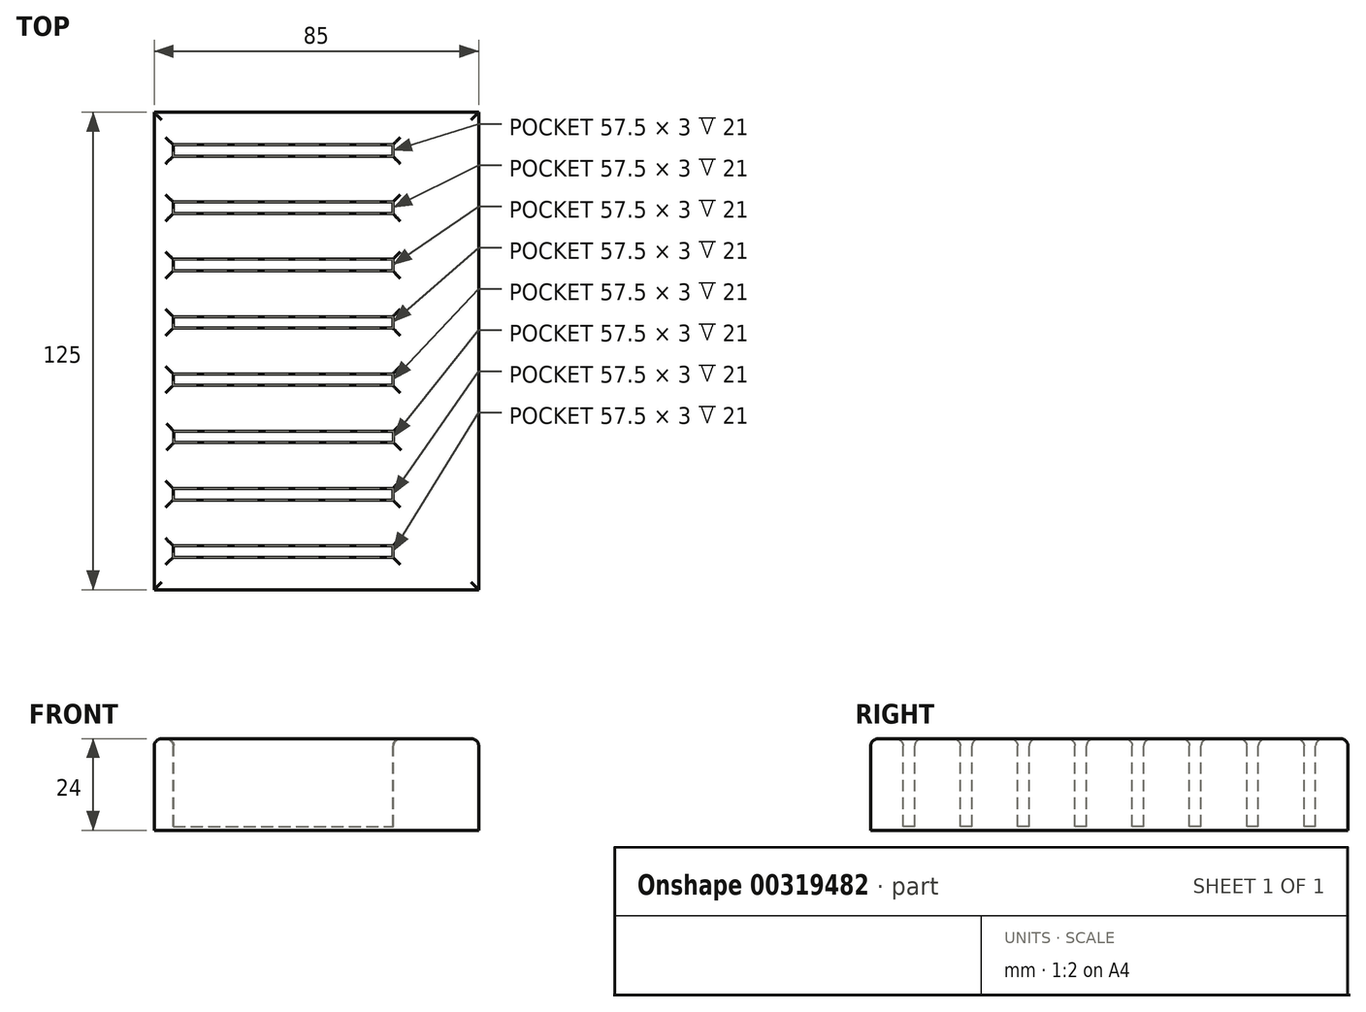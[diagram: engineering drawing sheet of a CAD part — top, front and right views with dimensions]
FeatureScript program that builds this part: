
annotation { "Feature Type Name" : "Feature", "Feature Type Description" : "" }
export const myFeature = defineFeature(function(context is Context, id is Id, definition is map)
    precondition{}
    {
        {
            var Q0;
            Q0=qCreatedBy(makeId("Top.planeOp"),FACE);
            var sketch = newSketch(context, id + "F0", { "sketchPlane" : qUnion([Q0])});
            skLineSegment(sketch, "E0.bottom", {"start": v(-49.85, 96.63) * mm, "end": v(35.15, 96.63) * mm});
            skLineSegment(sketch, "E0.top", {"start": v(-49.85, -28.37) * mm, "end": v(35.15, -28.37) * mm});
            skLineSegment(sketch, "E0.left", {"start": v(-49.85, 96.63) * mm, "end": v(-49.85, -28.37) * mm});
            skLineSegment(sketch, "E0.right", {"start": v(35.15, 96.63) * mm, "end": v(35.15, -28.37) * mm});
            skSolve(sketch);
        }
        {
            var Q0;
            Q0=makeQuery(id+"F0.imprint","IMPRINT",FACE,{"disambiguationData":[TD([[makeQuery(id+"F0.imprint","IMPRINT",EDGE,{"derivedFrom":sQuery(id+"F0.wireOp",EDGE,"E0.bottom")}),-1.0]])]});
            var Q1;
            Q1=makeQuery(id+"F0.imprint","IMPRINT",FACE,{"disambiguationData":[TD([[makeQuery(id+"F0.imprint","IMPRINT",EDGE,{"derivedFrom":sQuery(id+"F0.wireOp",EDGE,"eXpO4zti-W6eb-gkUP-Bc0d-zbJJjk6ygzeg.bottom")}),-1.0]])]});
            var Q2;
            Q2=makeQuery(id+"F0.imprint","IMPRINT",FACE,{"disambiguationData":[TD([[makeQuery(id+"F0.imprint","IMPRINT",EDGE,{"derivedFrom":sQuery(id+"F0.wireOp",EDGE,"IiJkesfC-iyIp-GpGT-9vFS-BzQ84R5pHUzr.bottom")}),-1.0]])]});
            extrude(context, id + "F1", {"entities" : qUnion([Q0, Q1, Q2]), "depth" : 24 * mm});
        }
        {
            var Q0;
            Q0=makeQuery(id+"F1.opExtrude","CAP_FACE",FACE,{"disambiguationData":[OSD([sQuery(id+"F0.wireOp",EDGE,"E0.bottom"),sQuery(id+"F0.wireOp",EDGE,"E0.top"),sQuery(id+"F0.wireOp",EDGE,"E0.left"),sQuery(id+"F0.wireOp",EDGE,"E0.right")])],"isStart":false});
            var sketch = newSketch(context, id + "F2", { "sketchPlane" : qUnion([Q0])});
            skLineSegment(sketch, "E1.bottom", {"start": v(-44.85, -16.87) * mm, "end": v(12.65, -16.87) * mm});
            skLineSegment(sketch, "E1.top", {"start": v(-44.85, -19.87) * mm, "end": v(12.65, -19.87) * mm});
            skLineSegment(sketch, "E1.left", {"start": v(-44.85, -16.87) * mm, "end": v(-44.85, -19.87) * mm});
            skLineSegment(sketch, "E1.right", {"start": v(12.65, -16.87) * mm, "end": v(12.65, -19.87) * mm});
            skLineSegment(sketch, "E2.bottom", {"start": v(-44.87, -1.87) * mm, "end": v(12.63, -1.87) * mm});
            skLineSegment(sketch, "E2.top", {"start": v(-44.87, -4.87) * mm, "end": v(12.63, -4.87) * mm});
            skLineSegment(sketch, "E2.left", {"start": v(-44.87, -1.87) * mm, "end": v(-44.87, -4.87) * mm});
            skLineSegment(sketch, "E2.right", {"start": v(12.63, -1.87) * mm, "end": v(12.63, -4.87) * mm});
            skLineSegment(sketch, "E3.bottom", {"start": v(-44.66, 13.13) * mm, "end": v(12.84, 13.13) * mm});
            skLineSegment(sketch, "E3.top", {"start": v(-44.66, 10.13) * mm, "end": v(12.84, 10.13) * mm});
            skLineSegment(sketch, "E3.left", {"start": v(-44.66, 13.13) * mm, "end": v(-44.66, 10.13) * mm});
            skLineSegment(sketch, "E3.right", {"start": v(12.84, 13.13) * mm, "end": v(12.84, 10.13) * mm});
            skLineSegment(sketch, "E4.bottom", {"start": v(-44.85, 28.13) * mm, "end": v(12.65, 28.13) * mm});
            skLineSegment(sketch, "E4.top", {"start": v(-44.85, 25.13) * mm, "end": v(12.65, 25.13) * mm});
            skLineSegment(sketch, "E4.left", {"start": v(-44.85, 28.13) * mm, "end": v(-44.85, 25.13) * mm});
            skLineSegment(sketch, "E4.right", {"start": v(12.65, 28.13) * mm, "end": v(12.65, 25.13) * mm});
            skLineSegment(sketch, "E5.bottom", {"start": v(-44.85, 43.13) * mm, "end": v(12.65, 43.13) * mm});
            skLineSegment(sketch, "E5.top", {"start": v(-44.85, 40.13) * mm, "end": v(12.65, 40.13) * mm});
            skLineSegment(sketch, "E5.left", {"start": v(-44.85, 43.13) * mm, "end": v(-44.85, 40.13) * mm});
            skLineSegment(sketch, "E5.right", {"start": v(12.65, 43.13) * mm, "end": v(12.65, 40.13) * mm});
            skLineSegment(sketch, "E6.bottom", {"start": v(-44.85, 58.13) * mm, "end": v(12.65, 58.13) * mm});
            skLineSegment(sketch, "E6.top", {"start": v(-44.85, 55.13) * mm, "end": v(12.65, 55.13) * mm});
            skLineSegment(sketch, "E6.left", {"start": v(-44.85, 58.13) * mm, "end": v(-44.85, 55.13) * mm});
            skLineSegment(sketch, "E6.right", {"start": v(12.65, 58.13) * mm, "end": v(12.65, 55.13) * mm});
            skLineSegment(sketch, "E7.bottom", {"start": v(-44.85, 73.13) * mm, "end": v(12.65, 73.13) * mm});
            skLineSegment(sketch, "E7.top", {"start": v(-44.85, 70.13) * mm, "end": v(12.65, 70.13) * mm});
            skLineSegment(sketch, "E7.left", {"start": v(-44.85, 73.13) * mm, "end": v(-44.85, 70.13) * mm});
            skLineSegment(sketch, "E7.right", {"start": v(12.65, 73.13) * mm, "end": v(12.65, 70.13) * mm});
            skLineSegment(sketch, "E8.bottom", {"start": v(-44.85, 88.13) * mm, "end": v(12.65, 88.13) * mm});
            skLineSegment(sketch, "E8.top", {"start": v(-44.85, 85.13) * mm, "end": v(12.65, 85.13) * mm});
            skLineSegment(sketch, "E8.left", {"start": v(-44.85, 88.13) * mm, "end": v(-44.85, 85.13) * mm});
            skLineSegment(sketch, "E8.right", {"start": v(12.65, 88.13) * mm, "end": v(12.65, 85.13) * mm});
            skSolve(sketch);
        }
        {
            var Q0;
            Q0=makeQuery(id+"F2.imprint","IMPRINT",FACE,{"disambiguationData":[TD([[makeQuery(id+"F2.imprint","IMPRINT",EDGE,{"derivedFrom":sQuery(id+"F2.wireOp",EDGE,"yj92iIYZ-7Uuq-LLpB-xCTO-jwhjS4Wwiwas.bottom")}),-1.0]])]});
            var Q1;
            Q1=makeQuery(id+"F2.imprint","IMPRINT",FACE,{"disambiguationData":[TD([[makeQuery(id+"F2.imprint","IMPRINT",EDGE,{"derivedFrom":sQuery(id+"F2.wireOp",EDGE,"E1.bottom")}),-1.0]])]});
            var Q2;
            Q2=makeQuery(id+"F2.imprint","IMPRINT",FACE,{"disambiguationData":[TD([[makeQuery(id+"F2.imprint","IMPRINT",EDGE,{"derivedFrom":sQuery(id+"F2.wireOp",EDGE,"E2.bottom")}),-1.0]])]});
            var Q3;
            Q3=makeQuery(id+"F2.imprint","IMPRINT",FACE,{"disambiguationData":[TD([[makeQuery(id+"F2.imprint","IMPRINT",EDGE,{"derivedFrom":sQuery(id+"F2.wireOp",EDGE,"6c3d6b7c-aaf7-4bf9-aa00-7a1dd3ff97cf.bottom")}),-1.0]])]});
            var Q4;
            Q4=makeQuery(id+"F2.imprint","IMPRINT",FACE,{"disambiguationData":[TD([[makeQuery(id+"F2.imprint","IMPRINT",EDGE,{"derivedFrom":sQuery(id+"F2.wireOp",EDGE,"50188bc1-ddcb-4dd7-b74a-52671ef0af12.bottom")}),-1.0]])]});
            var Q5;
            Q5=makeQuery(id+"F2.imprint","IMPRINT",FACE,{"disambiguationData":[TD([[makeQuery(id+"F2.imprint","IMPRINT",EDGE,{"derivedFrom":sQuery(id+"F2.wireOp",EDGE,"40c54da7-0a9d-487e-a4c4-20ab9cb4bac7.bottom")}),-1.0]])]});
            var Q6;
            Q6=makeQuery(id+"F2.imprint","IMPRINT",FACE,{"disambiguationData":[TD([[makeQuery(id+"F2.imprint","IMPRINT",EDGE,{"derivedFrom":sQuery(id+"F2.wireOp",EDGE,"2c54d664-a705-4687-aeb6-1d6c2977d349.bottom")}),-1.0]])]});
            var Q7;
            Q7=makeQuery(id+"F2.imprint","IMPRINT",FACE,{"disambiguationData":[TD([[makeQuery(id+"F2.imprint","IMPRINT",EDGE,{"derivedFrom":sQuery(id+"F2.wireOp",EDGE,"37cae19a-1d6e-44c9-97dd-f8e5000e89ab.bottom")}),-1.0]])]});
            var Q8;
            Q8=makeQuery(id+"F2.imprint","IMPRINT",FACE,{"disambiguationData":[TD([[makeQuery(id+"F2.imprint","IMPRINT",EDGE,{"derivedFrom":sQuery(id+"F2.wireOp",EDGE,"b65af77c-a413-450f-8f38-1bad91a99a45.bottom")}),-1.0]])]});
            var Q9;
            Q9=makeQuery(id+"F2.imprint","IMPRINT",FACE,{"disambiguationData":[TD([[makeQuery(id+"F2.imprint","IMPRINT",EDGE,{"derivedFrom":sQuery(id+"F2.wireOp",EDGE,"7d05ea80-09af-4c06-bbdd-2276bf2f09b7.bottom")}),-1.0]])]});
            var Q10;
            Q10=makeQuery(id+"F2.imprint","IMPRINT",FACE,{"disambiguationData":[TD([[makeQuery(id+"F2.imprint","IMPRINT",EDGE,{"derivedFrom":sQuery(id+"F2.wireOp",EDGE,"01eb7785-34fb-4985-9cad-6e3e3be28db8.bottom")}),-1.0]])]});
            var Q11;
            Q11=makeQuery(id+"F2.imprint","IMPRINT",FACE,{"disambiguationData":[TD([[makeQuery(id+"F2.imprint","IMPRINT",EDGE,{"derivedFrom":sQuery(id+"F2.wireOp",EDGE,"7e82bba3-7e2f-4ee3-9ea2-689606380510.bottom")}),-1.0]])]});
            var Q12;
            Q12=makeQuery(id+"F2.imprint","IMPRINT",FACE,{"disambiguationData":[TD([[makeQuery(id+"F2.imprint","IMPRINT",EDGE,{"derivedFrom":sQuery(id+"F2.wireOp",EDGE,"E3.bottom")}),-1.0]])]});
            var Q13;
            Q13=makeQuery(id+"F2.imprint","IMPRINT",FACE,{"disambiguationData":[TD([[makeQuery(id+"F2.imprint","IMPRINT",EDGE,{"derivedFrom":sQuery(id+"F2.wireOp",EDGE,"E4.bottom")}),-1.0]])]});
            var Q14;
            Q14=makeQuery(id+"F2.imprint","IMPRINT",FACE,{"disambiguationData":[TD([[makeQuery(id+"F2.imprint","IMPRINT",EDGE,{"derivedFrom":sQuery(id+"F2.wireOp",EDGE,"E5.bottom")}),-1.0]])]});
            var Q15;
            Q15=makeQuery(id+"F2.imprint","IMPRINT",FACE,{"disambiguationData":[TD([[makeQuery(id+"F2.imprint","IMPRINT",EDGE,{"derivedFrom":sQuery(id+"F2.wireOp",EDGE,"E6.bottom")}),-1.0]])]});
            var Q16;
            Q16=makeQuery(id+"F2.imprint","IMPRINT",FACE,{"disambiguationData":[TD([[makeQuery(id+"F2.imprint","IMPRINT",EDGE,{"derivedFrom":sQuery(id+"F2.wireOp",EDGE,"E7.bottom")}),-1.0]])]});
            var Q17;
            Q17=makeQuery(id+"F2.imprint","IMPRINT",FACE,{"disambiguationData":[TD([[makeQuery(id+"F2.imprint","IMPRINT",EDGE,{"derivedFrom":sQuery(id+"F2.wireOp",EDGE,"E8.bottom")}),-1.0]])]});
            var Q18;
            Q18=makeQuery(id+"F2.imprint","IMPRINT",FACE,{"disambiguationData":[TD([[makeQuery(id+"F2.imprint","IMPRINT",EDGE,{"derivedFrom":sQuery(id+"F2.wireOp",EDGE,"efc62570-a1f0-4d1b-bca0-e349addd9173.bottom")}),-1.0]])]});
            var Q19;
            Q19=makeQuery(id+"F2.imprint","IMPRINT",FACE,{"disambiguationData":[TD([[makeQuery(id+"F2.imprint","IMPRINT",EDGE,{"derivedFrom":sQuery(id+"F2.wireOp",EDGE,"dca9b81b-4f38-4141-b403-f49ceaf93926.bottom")}),-1.0]])]});
            extrude(context, id + "F3", {"entities" : qUnion([Q0, Q1, Q2, Q3, Q4, Q5, Q6, Q7, Q8, Q9, Q10, Q11, Q12, Q13, Q14, Q15, Q16, Q17, Q18, Q19]), "operationType" : NewBodyOperationType.REMOVE, "oppositeDirection" : true, "depth" : 23 * mm});
        }
        {
            var Q0;
            Q0=makeQuery(id+"F3.boolean.opBoolean","COPY",EDGE,{"derivedFrom":makeQuery(id+"F3.opExtrude","CAP_EDGE",EDGE,{"disambiguationData":[OSD([sQuery(id+"F2.wireOp",EDGE,"E1.top")])],"isStart":true})});
            var Q1;
            Q1=makeQuery(id+"F3.boolean.opBoolean","COPY",EDGE,{"derivedFrom":makeQuery(id+"F3.opExtrude","CAP_EDGE",EDGE,{"disambiguationData":[OSD([sQuery(id+"F2.wireOp",EDGE,"E1.bottom")])],"isStart":true})});
            var Q2;
            Q2=makeQuery(id+"F3.boolean.opBoolean","COPY",EDGE,{"derivedFrom":makeQuery(id+"F3.opExtrude","CAP_EDGE",EDGE,{"disambiguationData":[OSD([sQuery(id+"F2.wireOp",EDGE,"E1.right")])],"isStart":true})});
            var Q3;
            Q3=makeQuery(id+"F3.boolean.opBoolean","COPY",EDGE,{"derivedFrom":makeQuery(id+"F3.opExtrude","CAP_EDGE",EDGE,{"disambiguationData":[OSD([sQuery(id+"F2.wireOp",EDGE,"E1.left")])],"isStart":true})});
            var Q4;
            Q4=makeQuery(id+"F3.boolean.opBoolean","COPY",EDGE,{"derivedFrom":makeQuery(id+"F3.opExtrude","CAP_EDGE",EDGE,{"disambiguationData":[OSD([sQuery(id+"F2.wireOp",EDGE,"yj92iIYZ-7Uuq-LLpB-xCTO-jwhjS4Wwiwas.bottom")])],"isStart":true})});
            var Q5;
            Q5=makeQuery(id+"F3.boolean.opBoolean","COPY",EDGE,{"derivedFrom":makeQuery(id+"F3.opExtrude","CAP_EDGE",EDGE,{"disambiguationData":[OSD([sQuery(id+"F2.wireOp",EDGE,"yj92iIYZ-7Uuq-LLpB-xCTO-jwhjS4Wwiwas.top")])],"isStart":true})});
            var Q6;
            Q6=makeQuery(id+"F3.boolean.opBoolean","COPY",EDGE,{"derivedFrom":makeQuery(id+"F3.opExtrude","CAP_EDGE",EDGE,{"disambiguationData":[OSD([sQuery(id+"F2.wireOp",EDGE,"yj92iIYZ-7Uuq-LLpB-xCTO-jwhjS4Wwiwas.left")])],"isStart":true})});
            var Q7;
            Q7=makeQuery(id+"F3.boolean.opBoolean","COPY",EDGE,{"derivedFrom":makeQuery(id+"F3.opExtrude","CAP_EDGE",EDGE,{"disambiguationData":[OSD([sQuery(id+"F2.wireOp",EDGE,"yj92iIYZ-7Uuq-LLpB-xCTO-jwhjS4Wwiwas.right")])],"isStart":true})});
            var Q8;
            Q8=makeQuery(id+"F3.boolean.opBoolean","COPY",EDGE,{"derivedFrom":makeQuery(id+"F3.opExtrude","CAP_EDGE",EDGE,{"disambiguationData":[OSD([sQuery(id+"F2.wireOp",EDGE,"E2.bottom")])],"isStart":true})});
            var Q9;
            Q9=makeQuery(id+"F3.boolean.opBoolean","COPY",EDGE,{"derivedFrom":makeQuery(id+"F3.opExtrude","CAP_EDGE",EDGE,{"disambiguationData":[OSD([sQuery(id+"F2.wireOp",EDGE,"E2.top")])],"isStart":true})});
            var Q10;
            Q10=makeQuery(id+"F3.boolean.opBoolean","COPY",EDGE,{"derivedFrom":makeQuery(id+"F3.opExtrude","CAP_EDGE",EDGE,{"disambiguationData":[OSD([sQuery(id+"F2.wireOp",EDGE,"E2.left")])],"isStart":true})});
            var Q11;
            Q11=makeQuery(id+"F3.boolean.opBoolean","COPY",EDGE,{"derivedFrom":makeQuery(id+"F3.opExtrude","CAP_EDGE",EDGE,{"disambiguationData":[OSD([sQuery(id+"F2.wireOp",EDGE,"E2.right")])],"isStart":true})});
            var Q12;
            Q12=makeQuery(id+"F3.boolean.opBoolean","COPY",EDGE,{"derivedFrom":makeQuery(id+"F3.opExtrude","CAP_EDGE",EDGE,{"disambiguationData":[OSD([sQuery(id+"F2.wireOp",EDGE,"6c3d6b7c-aaf7-4bf9-aa00-7a1dd3ff97cf.left")])],"isStart":true})});
            var Q13;
            Q13=makeQuery(id+"F3.boolean.opBoolean","COPY",EDGE,{"derivedFrom":makeQuery(id+"F3.opExtrude","CAP_EDGE",EDGE,{"disambiguationData":[OSD([sQuery(id+"F2.wireOp",EDGE,"6c3d6b7c-aaf7-4bf9-aa00-7a1dd3ff97cf.bottom")])],"isStart":true})});
            var Q14;
            Q14=makeQuery(id+"F3.boolean.opBoolean","COPY",EDGE,{"derivedFrom":makeQuery(id+"F3.opExtrude","CAP_EDGE",EDGE,{"disambiguationData":[OSD([sQuery(id+"F2.wireOp",EDGE,"6c3d6b7c-aaf7-4bf9-aa00-7a1dd3ff97cf.right")])],"isStart":true})});
            var Q15;
            Q15=makeQuery(id+"F3.boolean.opBoolean","COPY",EDGE,{"derivedFrom":makeQuery(id+"F3.opExtrude","CAP_EDGE",EDGE,{"disambiguationData":[OSD([sQuery(id+"F2.wireOp",EDGE,"6c3d6b7c-aaf7-4bf9-aa00-7a1dd3ff97cf.top")])],"isStart":true})});
            var Q16;
            Q16=makeQuery(id+"F3.boolean.opBoolean","COPY",EDGE,{"derivedFrom":makeQuery(id+"F3.opExtrude","CAP_EDGE",EDGE,{"disambiguationData":[OSD([sQuery(id+"F2.wireOp",EDGE,"50188bc1-ddcb-4dd7-b74a-52671ef0af12.top")])],"isStart":true})});
            var Q17;
            Q17=makeQuery(id+"F3.boolean.opBoolean","COPY",EDGE,{"derivedFrom":makeQuery(id+"F3.opExtrude","CAP_EDGE",EDGE,{"disambiguationData":[OSD([sQuery(id+"F2.wireOp",EDGE,"50188bc1-ddcb-4dd7-b74a-52671ef0af12.left")])],"isStart":true})});
            var Q18;
            Q18=makeQuery(id+"F3.boolean.opBoolean","COPY",EDGE,{"derivedFrom":makeQuery(id+"F3.opExtrude","CAP_EDGE",EDGE,{"disambiguationData":[OSD([sQuery(id+"F2.wireOp",EDGE,"50188bc1-ddcb-4dd7-b74a-52671ef0af12.bottom")])],"isStart":true})});
            var Q19;
            Q19=makeQuery(id+"F3.boolean.opBoolean","COPY",EDGE,{"derivedFrom":makeQuery(id+"F3.opExtrude","CAP_EDGE",EDGE,{"disambiguationData":[OSD([sQuery(id+"F2.wireOp",EDGE,"50188bc1-ddcb-4dd7-b74a-52671ef0af12.right")])],"isStart":true})});
            var Q20;
            Q20=makeQuery(id+"F3.boolean.opBoolean","COPY",EDGE,{"derivedFrom":makeQuery(id+"F3.opExtrude","CAP_EDGE",EDGE,{"disambiguationData":[OSD([sQuery(id+"F2.wireOp",EDGE,"40c54da7-0a9d-487e-a4c4-20ab9cb4bac7.top")])],"isStart":true})});
            var Q21;
            Q21=makeQuery(id+"F3.boolean.opBoolean","COPY",EDGE,{"derivedFrom":makeQuery(id+"F3.opExtrude","CAP_EDGE",EDGE,{"disambiguationData":[OSD([sQuery(id+"F2.wireOp",EDGE,"40c54da7-0a9d-487e-a4c4-20ab9cb4bac7.right")])],"isStart":true})});
            var Q22;
            Q22=makeQuery(id+"F3.boolean.opBoolean","COPY",EDGE,{"derivedFrom":makeQuery(id+"F3.opExtrude","CAP_EDGE",EDGE,{"disambiguationData":[OSD([sQuery(id+"F2.wireOp",EDGE,"40c54da7-0a9d-487e-a4c4-20ab9cb4bac7.bottom")])],"isStart":true})});
            var Q23;
            Q23=makeQuery(id+"F3.boolean.opBoolean","COPY",EDGE,{"derivedFrom":makeQuery(id+"F3.opExtrude","CAP_EDGE",EDGE,{"disambiguationData":[OSD([sQuery(id+"F2.wireOp",EDGE,"40c54da7-0a9d-487e-a4c4-20ab9cb4bac7.left")])],"isStart":true})});
            var Q24;
            Q24=makeQuery(id+"F3.boolean.opBoolean","COPY",EDGE,{"derivedFrom":makeQuery(id+"F3.opExtrude","CAP_EDGE",EDGE,{"disambiguationData":[OSD([sQuery(id+"F2.wireOp",EDGE,"2c54d664-a705-4687-aeb6-1d6c2977d349.left")])],"isStart":true})});
            var Q25;
            Q25=makeQuery(id+"F3.boolean.opBoolean","COPY",EDGE,{"derivedFrom":makeQuery(id+"F3.opExtrude","CAP_EDGE",EDGE,{"disambiguationData":[OSD([sQuery(id+"F2.wireOp",EDGE,"2c54d664-a705-4687-aeb6-1d6c2977d349.bottom")])],"isStart":true})});
            var Q26;
            Q26=makeQuery(id+"F1.opExtrude","CAP_FACE",FACE,{"disambiguationData":[OSD([sQuery(id+"F0.wireOp",EDGE,"E0.bottom"),sQuery(id+"F0.wireOp",EDGE,"E0.top"),sQuery(id+"F0.wireOp",EDGE,"E0.left"),sQuery(id+"F0.wireOp",EDGE,"E0.right")])],"isStart":false});
            var Q27;
            Q27=makeQuery(id+"F3.boolean.opBoolean","COPY",EDGE,{"derivedFrom":makeQuery(id+"F3.opExtrude","CAP_EDGE",EDGE,{"disambiguationData":[OSD([sQuery(id+"F2.wireOp",EDGE,"2c54d664-a705-4687-aeb6-1d6c2977d349.right")])],"isStart":true})});
            fillet(context, id + "F4", {"entities" : qUnion([Q0, Q1, Q2, Q3, Q4, Q5, Q6, Q7, Q8, Q9, Q10, Q11, Q12, Q13, Q14, Q15, Q16, Q17, Q18, Q19, Q20, Q21, Q22, Q23, Q24, Q25, Q26, Q27]), "radius" : 2 * mm, "tangentPropagation" : true, "allowEdgeOverflow" : false});
        }
    });
